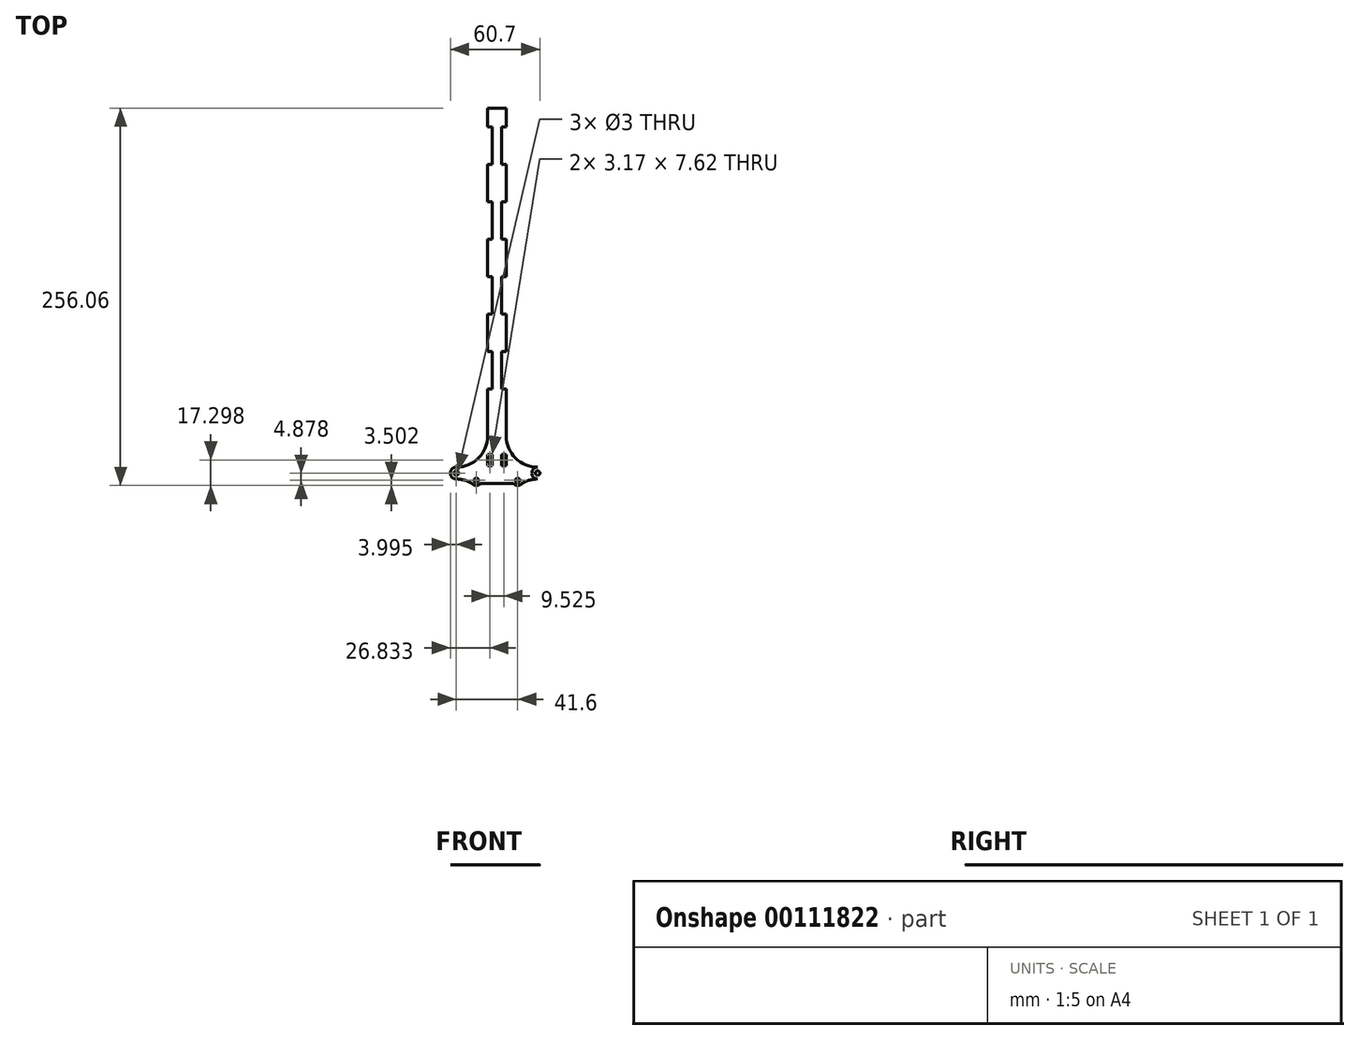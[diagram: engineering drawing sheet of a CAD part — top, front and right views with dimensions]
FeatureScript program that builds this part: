
annotation { "Feature Type Name" : "Feature", "Feature Type Description" : "" }
export const myFeature = defineFeature(function(context is Context, id is Id, definition is map)
    precondition{}
    {
        {
            var Q0;
            Q0=qCreatedBy(makeId("Top.planeOp"),FACE);
            var sketch = newSketch(context, id + "F0", { "sketchPlane" : qUnion([Q0])});
            skLineSegment(sketch, "E0", {"start": v(-45.33, 65.05) * mm, "end": v(-45.33, -65.05) * mm, "construction": true});
            skLineSegment(sketch, "E1", {"start": v(39.67, 65.05) * mm, "end": v(39.67, -65.05) * mm, "construction": true});
            skLineSegment(sketch, "E2", {"start": v(-86.73, 0) * mm, "end": v(86.73, 0) * mm, "construction": true});
            skLineSegment(sketch, "E3", {"start": v(0, 65.05) * mm, "end": v(0, -65.05) * mm, "construction": true});
            skPoint(sketch, "E4", {"position": v(0, 0) * mm});
            skCircle(sketch, "E5", {"center": v(-23.78, 15.33) * mm, "radius": 1.5 * mm, "construction": true});
            skCircle(sketch, "E6", {"center": v(4.22, 21.83) * mm, "radius": 1.5 * mm, "construction": true});
            skCircle(sketch, "E7", {"center": v(-23.78, 21.83) * mm, "radius": 1.5 * mm, "construction": true});
            skCircle(sketch, "E8", {"center": v(4.22, 15.33) * mm, "radius": 1.5 * mm, "construction": true});
            skCircle(sketch, "E9", {"center": v(17.22, 26.92) * mm, "radius": 1.5 * mm, "construction": true});
            skCircle(sketch, "E10", {"center": v(20.17, 28.73) * mm, "radius": 1.5 * mm, "construction": true});
            skCircle(sketch, "E11", {"center": v(22.93, 30.25) * mm, "radius": 1.5 * mm, "construction": true});
            skCircle(sketch, "E12", {"center": v(26.16, 31.49) * mm, "radius": 1.5 * mm, "construction": true});
            skCircle(sketch, "E13", {"center": v(-40.24, 28.92) * mm, "radius": 1.5 * mm, "construction": true});
            skCircle(sketch, "E14", {"center": v(-43.38, 30.44) * mm, "radius": 1.5 * mm, "construction": true});
            skCircle(sketch, "E15", {"center": v(-46.33, 31.87) * mm, "radius": 1.5 * mm, "construction": true});
            skLineSegment(sketch, "E16", {"start": v(-23.78, 21.83) * mm, "end": v(4.22, 21.83) * mm, "construction": true});
            skLineSegment(sketch, "E17", {"start": v(-9.78, 21.83) * mm, "end": v(-9.78, 11.7) * mm, "construction": true});
            skLineSegment(sketch, "E18", {"start": v(-9.78, 21.83) * mm, "end": v(-9.78, 130.8) * mm});
            skLineSegment(sketch, "E19.bottom", {"start": v(-16.13, 20.39) * mm, "end": v(-3.43, 20.39) * mm});
            skLineSegment(sketch, "E19.top", {"start": v(-16.13, 274.39) * mm, "end": v(-3.43, 274.39) * mm});
            skLineSegment(sketch, "E19.left", {"start": v(-16.13, 20.39) * mm, "end": v(-16.13, 274.39) * mm});
            skLineSegment(sketch, "E19.right", {"start": v(-3.43, 20.39) * mm, "end": v(-3.43, 274.39) * mm});
            skPoint(sketch, "E20", {"position": v(-9.78, 20.39) * mm});
            skCircle(sketch, "E21", {"center": v(-37.38, 26.71) * mm, "radius": 4 * mm});
            skArc(sketch, "E22", {"start": v(-37.38, 30.71) * mm, "mid": v(-22.36, 36.93) * mm, "end": v(-16.13, 51.96) * mm});
            skCircle(sketch, "E23", {"center": v(-23.78, 21.83) * mm, "radius": 1.5 * mm});
            skCircle(sketch, "E24", {"center": v(-23.78, 15.33) * mm, "radius": 1.5 * mm});
            skCircle(sketch, "E25", {"center": v(4.22, 21.83) * mm, "radius": 1.5 * mm});
            skCircle(sketch, "E26", {"center": v(4.22, 15.33) * mm, "radius": 1.5 * mm});
            skCircle(sketch, "E27", {"center": v(-37.38, 26.71) * mm, "radius": 1.5 * mm});
            skLineSegment(sketch, "E28", {"start": v(-20.24, 19.68) * mm, "end": v(0.67, 19.68) * mm});
            skPoint(sketch, "E29", {"position": v(-9.78, 19.68) * mm});
            skLineSegment(sketch, "E30", {"start": v(-37.38, 26.71) * mm, "end": v(-9.78, 26.71) * mm, "construction": true});
            skArc(sketch, "E31.MirrorCS", {"start": v(17.82, 30.71) * mm, "mid": v(2.79, 36.93) * mm, "end": v(-3.43, 51.96) * mm});
            skCircle(sketch, "E32.MirrorC", {"center": v(17.82, 26.71) * mm, "radius": 4 * mm});
            skLineSegment(sketch, "E33.bottom", {"start": v(-16.13, 261.69) * mm, "end": v(-12.96, 261.69) * mm});
            skLineSegment(sketch, "E33.top", {"start": v(-16.13, 236.29) * mm, "end": v(-12.96, 236.29) * mm});
            skLineSegment(sketch, "E33.left", {"start": v(-16.13, 261.69) * mm, "end": v(-16.13, 236.29) * mm});
            skLineSegment(sketch, "E33.right", {"start": v(-12.96, 261.69) * mm, "end": v(-12.96, 236.29) * mm});
            skLineSegment(sketch, "E34.0.1.0", {"start": v(-16.13, 210.89) * mm, "end": v(-12.96, 210.89) * mm});
            skLineSegment(sketch, "E34.0.1.1", {"start": v(-12.96, 210.89) * mm, "end": v(-12.96, 185.49) * mm});
            skLineSegment(sketch, "E34.0.1.2", {"start": v(-16.13, 210.89) * mm, "end": v(-16.13, 185.49) * mm});
            skLineSegment(sketch, "E34.0.1.3", {"start": v(-16.13, 185.49) * mm, "end": v(-12.96, 185.49) * mm});
            skLineSegment(sketch, "E34.0.2.0", {"start": v(-16.13, 160.09) * mm, "end": v(-12.96, 160.09) * mm});
            skLineSegment(sketch, "E34.0.2.1", {"start": v(-12.96, 160.09) * mm, "end": v(-12.96, 134.69) * mm});
            skLineSegment(sketch, "E34.0.2.2", {"start": v(-16.13, 160.09) * mm, "end": v(-16.13, 134.69) * mm});
            skLineSegment(sketch, "E34.0.2.3", {"start": v(-16.13, 134.69) * mm, "end": v(-12.96, 134.69) * mm});
            skLineSegment(sketch, "E34.0.3.0", {"start": v(-16.13, 109.29) * mm, "end": v(-12.96, 109.29) * mm});
            skLineSegment(sketch, "E34.0.3.1", {"start": v(-12.96, 109.29) * mm, "end": v(-12.96, 83.89) * mm});
            skLineSegment(sketch, "E34.0.3.2", {"start": v(-16.13, 109.29) * mm, "end": v(-16.13, 83.89) * mm});
            skLineSegment(sketch, "E34.0.3.3", {"start": v(-16.13, 83.89) * mm, "end": v(-12.96, 83.89) * mm});
            skLineSegment(sketch, "E34.1.0.0", {"start": v(-6.6, 261.69) * mm, "end": v(-3.43, 261.69) * mm});
            skLineSegment(sketch, "E34.1.0.1", {"start": v(-3.43, 261.69) * mm, "end": v(-3.43, 236.29) * mm});
            skLineSegment(sketch, "E34.1.0.2", {"start": v(-6.6, 261.69) * mm, "end": v(-6.6, 236.29) * mm});
            skLineSegment(sketch, "E34.1.0.3", {"start": v(-6.6, 236.29) * mm, "end": v(-3.43, 236.29) * mm});
            skLineSegment(sketch, "E34.1.1.0", {"start": v(-6.6, 210.89) * mm, "end": v(-3.43, 210.89) * mm});
            skLineSegment(sketch, "E34.1.1.1", {"start": v(-3.43, 210.89) * mm, "end": v(-3.43, 185.49) * mm});
            skLineSegment(sketch, "E34.1.1.2", {"start": v(-6.6, 210.89) * mm, "end": v(-6.6, 185.49) * mm});
            skLineSegment(sketch, "E34.1.1.3", {"start": v(-6.6, 185.49) * mm, "end": v(-3.43, 185.49) * mm});
            skLineSegment(sketch, "E34.1.2.0", {"start": v(-6.6, 160.09) * mm, "end": v(-3.43, 160.09) * mm});
            skLineSegment(sketch, "E34.1.2.1", {"start": v(-3.43, 160.09) * mm, "end": v(-3.43, 134.69) * mm});
            skLineSegment(sketch, "E34.1.2.2", {"start": v(-6.6, 160.09) * mm, "end": v(-6.6, 134.69) * mm});
            skLineSegment(sketch, "E34.1.2.3", {"start": v(-6.6, 134.69) * mm, "end": v(-3.43, 134.69) * mm});
            skLineSegment(sketch, "E34.1.3.0", {"start": v(-6.6, 109.29) * mm, "end": v(-3.43, 109.29) * mm});
            skLineSegment(sketch, "E34.1.3.1", {"start": v(-3.43, 109.29) * mm, "end": v(-3.43, 83.89) * mm});
            skLineSegment(sketch, "E34.1.3.2", {"start": v(-6.6, 109.29) * mm, "end": v(-6.6, 83.89) * mm});
            skLineSegment(sketch, "E34.1.3.3", {"start": v(-6.6, 83.89) * mm, "end": v(-3.43, 83.89) * mm});
            skLineSegment(sketch, "E34.direction1", {"start": v(-16.13, 261.69) * mm, "end": v(-6.6, 261.69) * mm, "construction": true});
            skLineSegment(sketch, "E34.direction2", {"start": v(-16.13, 261.69) * mm, "end": v(-16.13, 210.89) * mm, "construction": true});
            skCircle(sketch, "E35.MirrorC", {"center": v(17.82, 26.71) * mm, "radius": 1.5 * mm});
            skLineSegment(sketch, "E36.bottom", {"start": v(-16.13, 39.44) * mm, "end": v(-12.96, 39.44) * mm});
            skLineSegment(sketch, "E36.top", {"start": v(-16.13, 31.82) * mm, "end": v(-12.96, 31.82) * mm});
            skLineSegment(sketch, "E36.left", {"start": v(-16.13, 39.44) * mm, "end": v(-16.13, 31.82) * mm});
            skLineSegment(sketch, "E36.right", {"start": v(-12.96, 39.44) * mm, "end": v(-12.96, 31.82) * mm});
            skLineSegment(sketch, "E37.MirrorCS", {"start": v(-6.6, 39.44) * mm, "end": v(-6.6, 31.82) * mm});
            skLineSegment(sketch, "E38.MirrorCS", {"start": v(-3.43, 39.44) * mm, "end": v(-6.6, 39.44) * mm});
            skLineSegment(sketch, "E39.MirrorCS", {"start": v(-3.43, 31.82) * mm, "end": v(-6.6, 31.82) * mm});
            skCircle(sketch, "E40", {"center": v(4.22, 21.83) * mm, "radius": 3.5 * mm});
            skCircle(sketch, "E41.MirrorC", {"center": v(-23.78, 21.83) * mm, "radius": 3.5 * mm});
            skArc(sketch, "E42", {"start": v(-25.83, 18.99) * mm, "mid": v(-31.31, 21.76) * mm, "end": v(-37.38, 22.71) * mm});
            skArc(sketch, "E43", {"start": v(-20.24, 19.68) * mm, "mid": v(-20.9, 19.56) * mm, "end": v(-21.46, 19.22) * mm});
            skArc(sketch, "E44.MirrorCS", {"start": v(6.26, 18.99) * mm, "mid": v(11.74, 21.76) * mm, "end": v(17.82, 22.71) * mm});
            skArc(sketch, "E45.MirrorCS", {"start": v(0.67, 19.68) * mm, "mid": v(1.32, 19.56) * mm, "end": v(1.9, 19.22) * mm});
            skSolve(sketch);
        }
        {
            var Q0;
            Q0=makeQuery(id+"F0.imprint","IMPRINT",FACE,{"disambiguationData":[TD([[makeQuery(id+"F0.imprint","IMPRINT",EDGE,{"derivedFrom":sQuery(id+"F0.wireOp",EDGE,"E27")}),-1.0]])]});
            var Q1;
            Q1=makeQuery(id+"F0.imprint","IMPRINT",FACE,{"disambiguationData":[TD([[makeQuery(id+"F0.imprint","IMPRINT",EDGE,{"derivedFrom":sQuery(id+"F0.wireOp",EDGE,"RaBLFpKa-HNen-WNo9-ZVeC-zLP7eX3bLMMK")}),-1.0]])]});
            var Q2;
            {var subQ1=sQuery(id+"F0.wireOp",EDGE,"E19.bottom");Q2=makeQuery(id+"F0.imprint","IMPRINT",FACE,{"disambiguationData":[TD([[makeQuery(id+"F0.imprint","IMPRINT",EDGE,{"derivedFrom":subQ1}),-1.0]])]});}
            var Q3;
            {var subQ21=sQuery(id+"F0.wireOp",EDGE,"E19.bottom");Q3=makeQuery(id+"F0.imprint","IMPRINT",FACE,{"disambiguationData":[TD([[makeQuery(id+"F0.imprint","IMPRINT",EDGE,{"derivedFrom":subQ21}),1.0]])]});}
            var Q4;
            {var subQ1=sQuery(id+"F0.wireOp",EDGE,"E19.bottom");Q4=makeQuery(id+"F0.imprint","IMPRINT",FACE,{"disambiguationData":[TD([[makeQuery(id+"F0.imprint","IMPRINT",EDGE,{"derivedFrom":subQ1}),-1.0]])]});}
            var Q5;
            Q5=makeQuery(id+"F0.imprint","IMPRINT",FACE,{"disambiguationData":[TD([[makeQuery(id+"F0.imprint","IMPRINT",EDGE,{"derivedFrom":sQuery(id+"F0.wireOp",EDGE,"E35.MirrorC")}),1.0]])]});
            var Q6;
            Q6=makeQuery(id+"F0.imprint","IMPRINT",FACE,{"disambiguationData":[TD([[makeQuery(id+"F0.imprint","IMPRINT",EDGE,{"derivedFrom":sQuery(id+"F0.wireOp",EDGE,"E23")}),-1.0]])]});
            var Q7;
            Q7=makeQuery(id+"F0.imprint","IMPRINT",FACE,{"disambiguationData":[TD([[makeQuery(id+"F0.imprint","IMPRINT",EDGE,{"derivedFrom":sQuery(id+"F0.wireOp",EDGE,"E25")}),-1.0]])]});
            extrude(context, id + "F1", {"entities" : qUnion([Q0, Q1, Q2, Q3, Q4, Q5, Q6, Q7]), "depth" : 1 / 203.2 * mm});
        }
    });
